# Revit family: QF_MACOM_MLXX_70XXXP
name_source: partatom
category: Equipamento especial
units: mm (PartAtom-declared; Revit-internal decimal feet)

## family parameters
Com base no plano de trabalho = Não
Compartilhado = Não
Corte com vazios quando carregada = Não
Cota do conector redondo = Utilizar diâmetro
Número OmniClass = 23.40.40.14
Ponto de cálculo do ambiente = Não
Sempre na vertical = Sim
Tipo de parte = Normal
Título OmniClass = Food Service Equipment

## types (14) — shared parameters
Depth Actual = 700,000 mm
Elevação padrão = 0,000 mm
Fabricante = MACOM
Height Actual = 900,000 mm
URL = https://www.acosmacom.com.br

## per-type parameters (varying)
| type | Back Border | Descrição | Foot w/ +2000 mm | Length Actual | Stand |
| MLTP-70250P | Sim | MESA LISA INOX PREMIUM MACOM ESP.TRASEIRO + PRATEL.INFERIOR 2500X700X900mm | Sim | 2500,000 mm | Sim |
| MLN-7070P | Não | MESA LISA INOX PREMIUM MACOM CENTRO 700X700X900mm | Não | 700,000 mm | Não |
| MLN-70140P | Não | MESA LISA INOX PREMIUM MACOM CENTRO 1400X700X900mm | Não | 1400,000 mm | Não |
| MLN-70180P | Não | MESA LISA INOX PREMIUM MACOM CENTRO 1800X700X900mm | Não | 1800,000 mm | Não |
| MLN-70200P | Não | MESA LISA INOX PREMIUM MACOM CENTRO 2000X700X900mm | Não | 2000,000 mm | Não |
| MLT-7070P | Sim | MESA LISA INOX PREMIUM MACOM ESP.TRASEIRO 700X700X900mm | Não | 700,000 mm | Não |
| MLT-70140P | Sim | MESA LISA INOX PREMIUM MACOM ESP.TRASEIRO 1400X700X900mm | Não | 1400,000 mm | Não |
| MLT-70180P | Sim | MESA LISA INOX PREMIUM MACOM ESP.TRASEIRO 1800X700X900mm | Não | 1800,000 mm | Não |
| MLT-70200P | Sim | MESA LISA INOX PREMIUM MACOM ESP.TRASEIRO 2000X700X900mm | Não | 2000,000 mm | Não |
| MLT-70250P | Sim | MESA LISA INOX PREMIUM MACOM ESP.TRASEIRO 2500X700X900mm | Sim | 2500,000 mm | Não |
| MLTP-7070P | Sim | MESA LISA INOX PREMIUM MACOM ESP.TRASEIRO + PRATEL.INFERIOR 700X700X900mm | Não | 700,000 mm | Sim |
| MLTP-70140P | Sim | MESA LISA INOX PREMIUM MACOM ESP.TRASEIRO + PRATEL.INFERIOR 1400X700X900mm | Não | 1400,000 mm | Sim |
| MLTP-70180P | Sim | MESA LISA INOX PREMIUM MACOM ESP.TRASEIRO + PRATEL.INFERIOR 1800X700X900mm | Não | 1800,000 mm | Sim |
| MLTP-70200P | Sim | MESA LISA INOX PREMIUM MACOM ESP.TRASEIRO + PRATEL.INFERIOR 2000X700X900mm | Não | 2000,000 mm | Sim |

note: column(s) folded — value = type name in every type: Modelo
